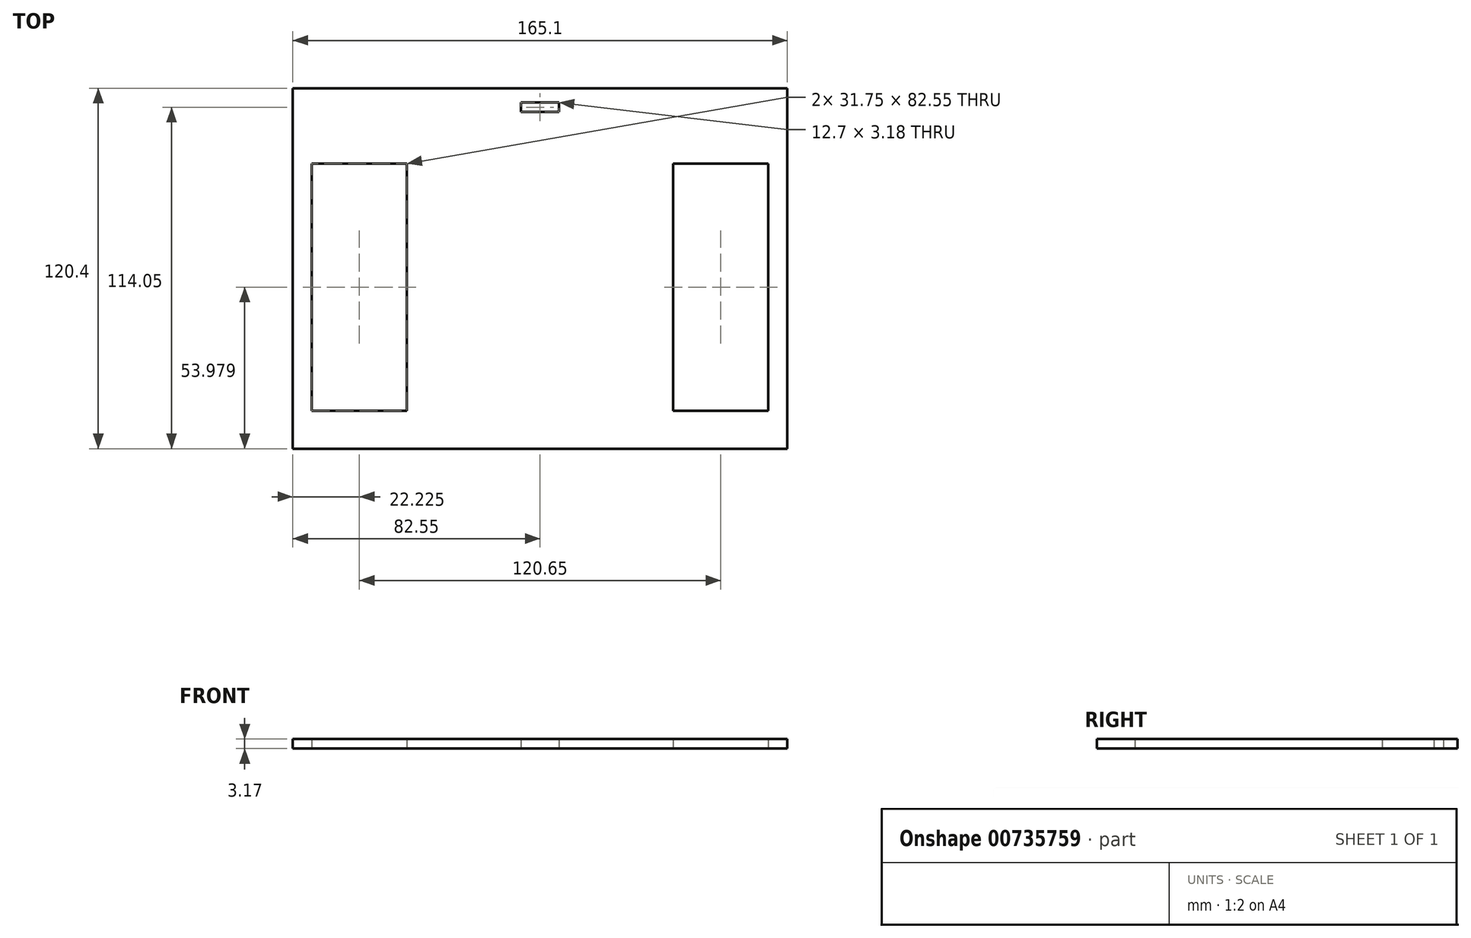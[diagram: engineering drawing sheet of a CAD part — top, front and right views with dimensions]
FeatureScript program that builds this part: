
annotation { "Feature Type Name" : "Feature", "Feature Type Description" : "" }
export const myFeature = defineFeature(function(context is Context, id is Id, definition is map)
    precondition{}
    {
        {
            var Q0;
            Q0=qCreatedBy(makeId("Top.planeOp"),FACE);
            var sketch = newSketch(context, id + "F0", { "sketchPlane" : qUnion([Q0])});
            skLineSegment(sketch, "E0.top", {"start": v(0, -120.4) * mm, "end": v(165.1, -120.4) * mm});
            skLineSegment(sketch, "E0.left", {"start": v(0, -12.7) * mm, "end": v(0, -120.4) * mm});
            skLineSegment(sketch, "E0.right", {"start": v(165.1, -12.7) * mm, "end": v(165.1, -120.4) * mm});
            skPoint(sketch, "E1", {"position": v(0, -12.7) * mm});
            skPoint(sketch, "E2", {"position": v(165.1, -12.7) * mm});
            skLineSegment(sketch, "E3", {"start": v(0, -12.7) * mm, "end": v(165.1, -12.7) * mm});
            skPoint(sketch, "E4", {"position": v(82.55, -12.7) * mm});
            skPoint(sketch, "E5", {"position": v(0, -69.85) * mm});
            skPoint(sketch, "E6", {"position": v(0, -37.85) * mm});
            skPoint(sketch, "E7", {"position": v(0, 12.95) * mm});
            skPoint(sketch, "E8", {"position": v(0, -25.4) * mm});
            skPoint(sketch, "E9", {"position": v(0, -114.3) * mm});
            skPoint(sketch, "E10", {"position": v(6.35, -37.85) * mm});
            skLineSegment(sketch, "E11", {"start": v(6.35, -37.85) * mm, "end": v(38.1, -37.85) * mm});
            skLineSegment(sketch, "E12", {"start": v(38.1, -37.85) * mm, "end": v(38.1, -120.4) * mm});
            skLineSegment(sketch, "E13", {"start": v(6.35, -37.85) * mm, "end": v(6.35, -120.4) * mm});
            skPoint(sketch, "E14", {"position": v(158.75, -37.85) * mm});
            skPoint(sketch, "E15", {"position": v(165.1, -37.85) * mm});
            skLineSegment(sketch, "E16", {"start": v(158.75, -37.85) * mm, "end": v(158.75, -120.4) * mm});
            skLineSegment(sketch, "E17", {"start": v(158.75, -37.85) * mm, "end": v(127, -37.85) * mm});
            skLineSegment(sketch, "E18", {"start": v(127, -37.85) * mm, "end": v(127, -120.4) * mm});
            skLineSegment(sketch, "E19.top", {"start": v(0, -133.1) * mm, "end": v(165.1, -133.1) * mm});
            skLineSegment(sketch, "E19.left", {"start": v(0, -120.4) * mm, "end": v(0, -133.1) * mm});
            skLineSegment(sketch, "E19.right", {"start": v(165.1, -120.4) * mm, "end": v(165.1, -133.1) * mm});
            skPoint(sketch, "E20.orphan", {"position": v(0, 0) * mm});
            skPoint(sketch, "E21", {"position": v(82.55, -19.05) * mm});
            skLineSegment(sketch, "E22.bottom", {"start": v(88.9, -20.64) * mm, "end": v(76.2, -20.64) * mm});
            skLineSegment(sketch, "E22.top", {"start": v(88.9, -17.46) * mm, "end": v(76.2, -17.46) * mm});
            skLineSegment(sketch, "E22.left", {"start": v(88.9, -20.64) * mm, "end": v(88.9, -17.46) * mm});
            skLineSegment(sketch, "E22.right", {"start": v(76.2, -20.64) * mm, "end": v(76.2, -17.46) * mm});
            skSolve(sketch);
        }
        {
            var Q0;
            Q0=makeQuery(id+"F0.imprint","IMPRINT",FACE,{"disambiguationData":[TD([[makeQuery(id+"F0.imprint","IMPRINT",EDGE,{"derivedFrom":sQuery(id+"F0.wireOp",EDGE,"E0.bottom")}),-1.0]])]});
            var Q1;
            {var subQ0=sQuery(id+"F0.wireOp",EDGE,"E0.top");Q1=makeQuery(id+"F0.imprint","IMPRINT",FACE,{"disambiguationData":[TD([[makeQuery(id+"F0.imprint","IMPRINT",EDGE,{"derivedFrom":subQ0}),1.0]])]});}
            var Q2;
            {var subQ7=sQuery(id+"F0.wireOp",EDGE,"E3");Q2=makeQuery(id+"F0.imprint","IMPRINT",FACE,{"disambiguationData":[TD([[makeQuery(id+"F0.imprint","IMPRINT",EDGE,{"derivedFrom":subQ7}),-1.0]])]});}
            var Q3;
            Q3=makeQuery(id+"F0.imprint","IMPRINT",FACE,{"disambiguationData":[TD([[makeQuery(id+"F0.imprint","IMPRINT",EDGE,{"derivedFrom":sQuery(id+"F0.wireOp",EDGE,"E19.top")}),1.0]])]});
            extrude(context, id + "F1", {"entities" : qUnion([Q0, Q1, Q2, Q3]), "depth" : 3.17 * mm, "offsetDistance" : 25.4 * mm});
        }
    });
